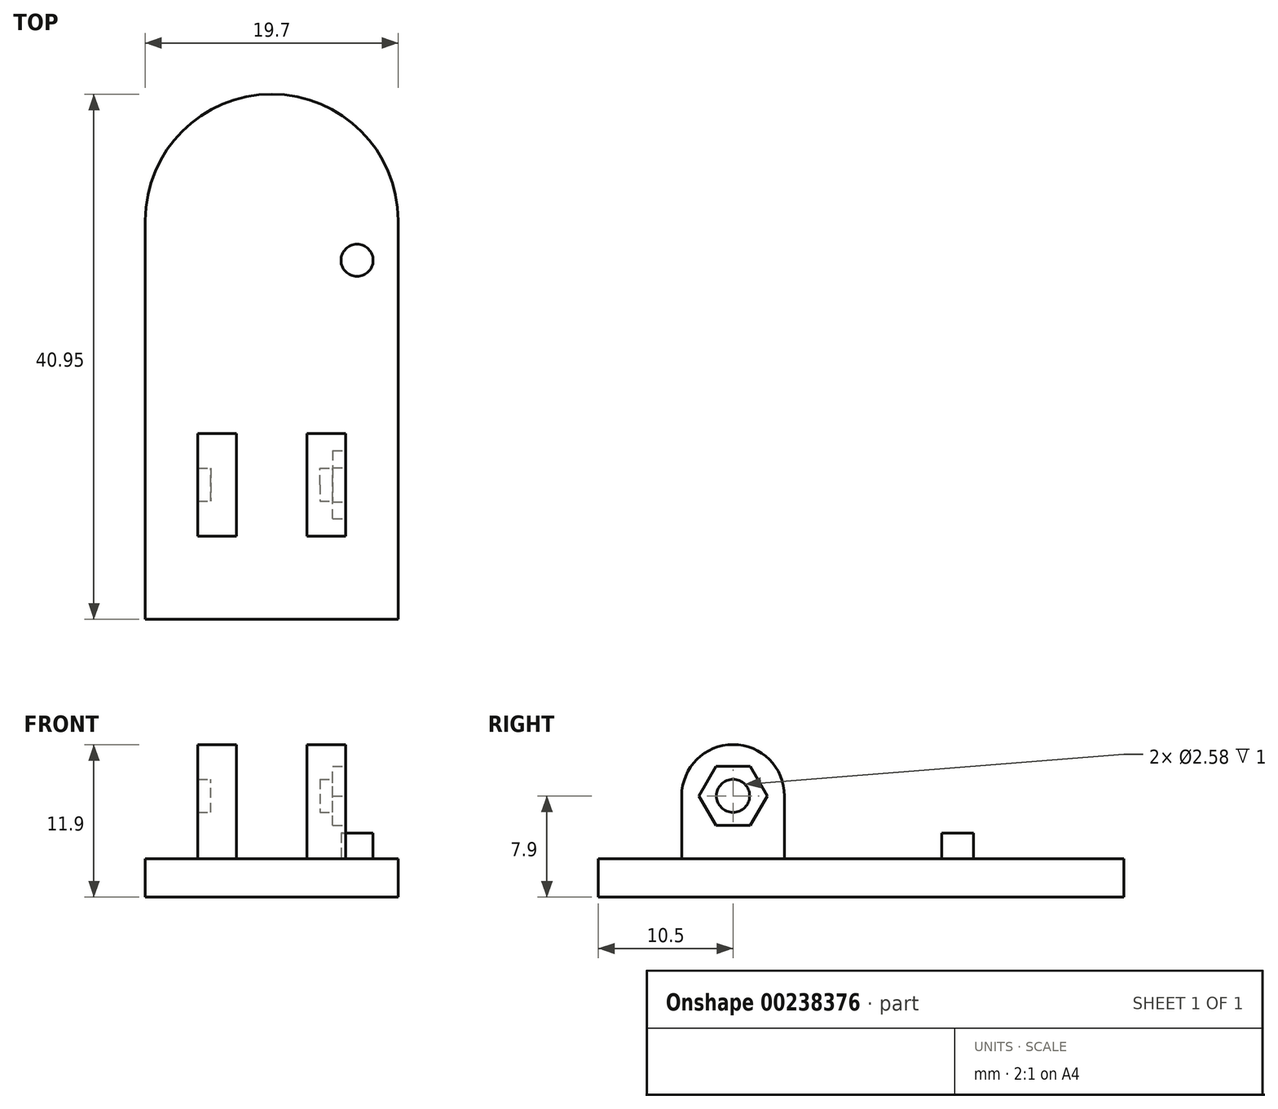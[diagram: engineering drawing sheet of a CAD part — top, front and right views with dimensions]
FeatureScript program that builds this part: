
annotation { "Feature Type Name" : "Feature", "Feature Type Description" : "" }
export const myFeature = defineFeature(function(context is Context, id is Id, definition is map)
    precondition{}
    {
        {
            var Q0;
            Q0=qCreatedBy(makeId("Top.planeOp"),FACE);
            var sketch = newSketch(context, id + "F0", { "sketchPlane" : qUnion([Q0])});
            skCircle(sketch, "E0", {"center": v(0, 0) * mm, "radius": 9.35 * mm});
            skLineSegment(sketch, "E1", {"start": v(-9.35, 0) * mm, "end": v(-9.35, -30.6) * mm});
            skLineSegment(sketch, "E2", {"start": v(9.35, 0) * mm, "end": v(9.35, -30.6) * mm});
            skLineSegment(sketch, "E3", {"start": v(9.35, -30.6) * mm, "end": v(-9.35, -30.6) * mm});
            skLineSegment(sketch, "E4", {"start": v(-5.75, -24.6) * mm, "end": v(-2.75, -24.6) * mm});
            skLineSegment(sketch, "E5.0", {"start": v(5.75, -16.6) * mm, "end": v(5.75, -24.6) * mm});
            skLineSegment(sketch, "E6.trimOffspring", {"start": v(-5.75, -16.6) * mm, "end": v(-5.75, -24.6) * mm});
            skLineSegment(sketch, "E7.0", {"start": v(-2.75, -16.6) * mm, "end": v(-2.75, -24.6) * mm});
            skLineSegment(sketch, "E8.0", {"start": v(2.75, -16.6) * mm, "end": v(2.75, -24.6) * mm});
            skLineSegment(sketch, "E9.trimOffspring", {"start": v(2.75, -16.6) * mm, "end": v(5.75, -16.6) * mm});
            skPoint(sketch, "E10.orphan", {"position": v(9.35, -16.6) * mm});
            skPoint(sketch, "E11.trimOffspring.end.orphan", {"position": v(0, 9.35) * mm});
            skLineSegment(sketch, "E12.trimOffspring", {"start": v(2.75, -24.6) * mm, "end": v(5.75, -24.6) * mm});
            skPoint(sketch, "E13.start.orphan", {"position": v(0, -30.6) * mm});
            skPoint(sketch, "E14.orphan", {"position": v(-9.35, -24.6) * mm});
            skLineSegment(sketch, "E15", {"start": v(-5.75, -16.6) * mm, "end": v(-2.75, -16.6) * mm});
            skSolve(sketch);
        }
        {
            var Q0;
            Q0=makeQuery(id+"F0.imprint","IMPRINT",FACE,{"disambiguationData":[TD([[makeQuery(id+"F0.imprint","IMPRINT",EDGE,{"derivedFrom":sQuery(id+"F0.wireOp",EDGE,"E5.0")}),-1.0]])]});
            var Q1;
            {var subQ0=sQuery(id+"F0.wireOp",EDGE,"E0");var subQ1=makeQuery(id+"F0.imprint","INTERSECT",VERTEX,{"derivedFrom":[subQ0,sQuery(id+"F0.wireOp",EDGE,"E1")]});Q1=makeQuery(id+"F0.imprint","IMPRINT",FACE,{"disambiguationData":[TD([[makeQuery(id+"F0.imprint","IMPRINT",EDGE,{"disambiguationData":[TD([[subQ1,1.0]])],"derivedFrom":subQ0}),1.0]])]});}
            var Q2;
            {var subQ1=sQuery(id+"F0.wireOp",EDGE,"E1");Q2=makeQuery(id+"F0.imprint","IMPRINT",FACE,{"disambiguationData":[TD([[makeQuery(id+"F0.imprint","IMPRINT",EDGE,{"derivedFrom":subQ1}),1.0]])]});}
            var Q3;
            Q3=makeQuery(id+"F0.imprint","IMPRINT",FACE,{"disambiguationData":[TD([[makeQuery(id+"F0.imprint","IMPRINT",EDGE,{"derivedFrom":sQuery(id+"F0.wireOp",EDGE,"E4")}),1.0]])]});
            extrude(context, id + "F1", {"entities" : qUnion([Q0, Q1, Q2, Q3]), "oppositeDirection" : true, "depth" : 3 * mm});
        }
        {
            var Q0;
            Q0=makeQuery(id+"F0.imprint","IMPRINT",FACE,{"disambiguationData":[TD([[makeQuery(id+"F0.imprint","IMPRINT",EDGE,{"derivedFrom":sQuery(id+"F0.wireOp",EDGE,"E5.0")}),-1.0]])]});
            extrude(context, id + "F2", {"entities" : qUnion([Q0]), "operationType" : NewBodyOperationType.ADD, "depth" : 4.9 * mm});
        }
        {
            var Q0;
            Q0=makeQuery(id+"F0.imprint","IMPRINT",FACE,{"disambiguationData":[TD([[makeQuery(id+"F0.imprint","IMPRINT",EDGE,{"derivedFrom":sQuery(id+"F0.wireOp",EDGE,"E4")}),1.0]])]});
            extrude(context, id + "F3", {"entities" : qUnion([Q0]), "operationType" : NewBodyOperationType.ADD, "depth" : 4.9 * mm});
        }
        {
            var Q0;
            Q0=makeQuery(id+"F3.opExtrude","SWEPT_FACE",FACE,{"disambiguationData":[OSD([sQuery(id+"F0.wireOp",EDGE,"E6.trimOffspring")])]});
            var sketch = newSketch(context, id + "F4", { "sketchPlane" : qUnion([Q0])});
            skCircle(sketch, "E16", {"center": v(20.6, 4.9) * mm, "radius": 4 * mm});
            skSolve(sketch);
        }
        {
            var Q0;
            {var subQ1=sQuery(id+"F0.wireOp",EDGE,"E6.trimOffspring");var subQ2=makeQuery(id+"F3.opExtrude","CAP_EDGE",EDGE,{"disambiguationData":[OSD([subQ1])],"isStart":false});Q0=makeQuery(id+"F4.imprint","IMPRINT",FACE,{"disambiguationData":[TD([[makeQuery(id+"F4.imprint","IMPRINT",EDGE,{"derivedFrom":subQ2}),1.0]])]});}
            extrude(context, id + "F5", {"entities" : qUnion([Q0]), "operationType" : NewBodyOperationType.ADD, "oppositeDirection" : true, "depth" : 3 * mm});
        }
        {
            var Q0;
            Q0=makeQuery(id+"F2.opExtrude","SWEPT_FACE",FACE,{"disambiguationData":[OSD([sQuery(id+"F0.wireOp",EDGE,"E5.0")])]});
            var sketch = newSketch(context, id + "F6", { "sketchPlane" : qUnion([Q0])});
            skCircle(sketch, "E17", {"center": v(-20.6, 4.9) * mm, "radius": 4 * mm});
            skCircle(sketch, "E18", {"center": v(-20.6, 4.9) * mm, "radius": 1.29 * mm});
            skCircle(sketch, "E19", {"center": v(-20.6, 4.9) * mm, "radius": 2.66 * mm, "construction": true});
            skLineSegment(sketch, "E20.0", {"start": v(-17.94, 4.9) * mm, "end": v(-19.27, 2.6) * mm});
            skLineSegment(sketch, "E20.1", {"start": v(-19.27, 2.6) * mm, "end": v(-21.93, 2.6) * mm});
            skLineSegment(sketch, "E20.2", {"start": v(-21.93, 2.6) * mm, "end": v(-23.26, 4.9) * mm});
            skLineSegment(sketch, "E20.3", {"start": v(-23.26, 4.9) * mm, "end": v(-21.93, 7.2) * mm});
            skLineSegment(sketch, "E20.4", {"start": v(-21.93, 7.2) * mm, "end": v(-19.27, 7.2) * mm});
            skLineSegment(sketch, "E20.5", {"start": v(-19.27, 7.2) * mm, "end": v(-17.94, 4.9) * mm});
            skSolve(sketch);
        }
        {
            var Q0;
            {var subQ1=sQuery(id+"F0.wireOp",EDGE,"E5.0");var subQ2=makeQuery(id+"F2.opExtrude","CAP_EDGE",EDGE,{"disambiguationData":[OSD([subQ1])],"isStart":false});Q0=makeQuery(id+"F6.imprint","IMPRINT",FACE,{"disambiguationData":[TD([[makeQuery(id+"F6.imprint","IMPRINT",EDGE,{"derivedFrom":subQ2}),-1.0]])]});}
            extrude(context, id + "F7", {"entities" : qUnion([Q0]), "operationType" : NewBodyOperationType.ADD, "oppositeDirection" : true, "depth" : 3 * mm});
        }
        {
            var Q0;
            {var subQ0=sQuery(id+"F6.wireOp",EDGE,"E18");var subQ1=makeQuery(id+"F2.opExtrude","CAP_EDGE",EDGE,{"disambiguationData":[OSD([sQuery(id+"F0.wireOp",EDGE,"E5.0")])],"isStart":false});var subQ2=makeQuery(id+"F6.imprint","INTERSECT",VERTEX,{"disambiguationData":[OD(0.0)],"derivedFrom":[subQ1,subQ0]});Q0=makeQuery(id+"F6.imprint","IMPRINT",FACE,{"disambiguationData":[TD([[makeQuery(id+"F6.imprint","IMPRINT",EDGE,{"disambiguationData":[TD([[subQ2,-1.0]])],"derivedFrom":subQ0}),1.0]])]});}
            var Q1;
            {var subQ0=sQuery(id+"F6.wireOp",EDGE,"E18");var subQ1=makeQuery(id+"F2.opExtrude","CAP_EDGE",EDGE,{"disambiguationData":[OSD([sQuery(id+"F0.wireOp",EDGE,"E5.0")])],"isStart":false});var subQ2=makeQuery(id+"F6.imprint","INTERSECT",VERTEX,{"disambiguationData":[OD(0.0)],"derivedFrom":[subQ1,subQ0]});Q1=makeQuery(id+"F6.imprint","IMPRINT",FACE,{"disambiguationData":[TD([[makeQuery(id+"F6.imprint","IMPRINT",EDGE,{"disambiguationData":[TD([[subQ2,1.0]])],"derivedFrom":subQ0}),1.0]])]});}
            extrude(context, id + "F8", {"entities" : qUnion([Q0, Q1]), "operationType" : NewBodyOperationType.REMOVE, "oppositeDirection" : true, "depth" : 25 * mm});
        }
        {
            var Q0;
            {var subQ0=sQuery(id+"F6.wireOp",EDGE,"E20.3");Q0=makeQuery(id+"F6.imprint","IMPRINT",FACE,{"disambiguationData":[TD([[makeQuery(id+"F6.imprint","IMPRINT",EDGE,{"derivedFrom":subQ0}),-1.0]])]});}
            var Q1;
            {var subQ1=sQuery(id+"F6.wireOp",EDGE,"E20.0");Q1=makeQuery(id+"F6.imprint","IMPRINT",FACE,{"disambiguationData":[TD([[makeQuery(id+"F6.imprint","IMPRINT",EDGE,{"derivedFrom":subQ1}),-1.0]])]});}
            extrude(context, id + "F9", {"entities" : qUnion([Q0, Q1]), "operationType" : NewBodyOperationType.REMOVE, "oppositeDirection" : true, "depth" : 1 * mm});
        }
        {
            var Q0;
            {var subQ0=sQuery(id+"F0.wireOp",EDGE,"E0");var subQ1=makeQuery(id+"F0.imprint","INTERSECT",VERTEX,{"derivedFrom":[subQ0,sQuery(id+"F0.wireOp",EDGE,"E1")]});Q0=makeQuery(id+"F0.imprint","IMPRINT",FACE,{"disambiguationData":[TD([[makeQuery(id+"F0.imprint","IMPRINT",EDGE,{"disambiguationData":[TD([[subQ1,1.0]])],"derivedFrom":subQ0}),1.0]])]});}
            var sketch = newSketch(context, id + "F10", { "sketchPlane" : qUnion([Q0])});
            skLineSegment(sketch, "E21.0", {"start": v(-9.35, 0) * mm, "end": v(-9.35, -30.6) * mm});
            skArc(sketch, "E21.1", {"start": v(9.35, 0) * mm, "mid": v(0, 9.35) * mm, "end": v(-9.35, 0) * mm});
            skLineSegment(sketch, "E21.2", {"start": v(9.35, 0) * mm, "end": v(9.35, -30.6) * mm});
            skLineSegment(sketch, "E21.3", {"start": v(9.35, -30.6) * mm, "end": v(-9.35, -30.6) * mm});
            skLineSegment(sketch, "E22.0", {"start": v(9.85, 0) * mm, "end": v(9.85, -31.1) * mm});
            skLineSegment(sketch, "E22.1", {"start": v(9.85, -31.1) * mm, "end": v(-9.85, -31.1) * mm});
            skLineSegment(sketch, "E22.2", {"start": v(-9.85, 0) * mm, "end": v(-9.85, -31.1) * mm});
            skArc(sketch, "E23.0", {"start": v(9.85, 0) * mm, "mid": v(0, 9.85) * mm, "end": v(-9.85, 0) * mm});
            skSolve(sketch);
        }
        {
            var Q0;
            Q0=makeQuery(id+"F10.imprint","IMPRINT",FACE,{"disambiguationData":[TD([[makeQuery(id+"F10.imprint","IMPRINT",EDGE,{"derivedFrom":sQuery(id+"F10.wireOp",EDGE,"E21.0")}),-1.0]])]});
            extrude(context, id + "F11", {"entities" : qUnion([Q0]), "operationType" : NewBodyOperationType.ADD, "oppositeDirection" : true, "depth" : 3 * mm});
        }
        {
            var Q0;
            Q0=makeQuery(id+"F5.boolean.opBoolean","MERGE",FACE,{"derivedFrom":[makeQuery(id+"F3.opExtrude","SWEPT_FACE",FACE,{"disambiguationData":[OSD([sQuery(id+"F0.wireOp",EDGE,"E7.0")])]}),makeQuery(id+"F5.opExtrude","CAP_FACE",FACE,{"disambiguationData":[OSD([sQuery(id+"F0.wireOp",EDGE,"E6.trimOffspring"),sQuery(id+"F4.wireOp",EDGE,"E16")])],"isStart":false})]});
            var sketch = newSketch(context, id + "F12", { "sketchPlane" : qUnion([Q0])});
            skCircle(sketch, "E24", {"center": v(-20.6, 4.9) * mm, "radius": 1.86 * mm});
            skSolve(sketch);
        }
        {
            var Q0;
            Q0 = qSketchRegion(id + "F12", true);
            extrude(context, id + "F13", {"entities" : qUnion([Q0]), "operationType" : NewBodyOperationType.ADD, "oppositeDirection" : true, "depth" : 1 * mm});
        }
        {
            var Q0;
            Q0=makeQuery(id+"F7.boolean.opBoolean","MERGE",FACE,{"derivedFrom":[makeQuery(id+"F2.opExtrude","SWEPT_FACE",FACE,{"disambiguationData":[OSD([sQuery(id+"F0.wireOp",EDGE,"E8.0")])]}),makeQuery(id+"F7.opExtrude","CAP_FACE",FACE,{"disambiguationData":[OSD([sQuery(id+"F0.wireOp",EDGE,"E5.0"),sQuery(id+"F6.wireOp",EDGE,"E17"),sQuery(id+"F6.wireOp",EDGE,"E18")])],"isStart":false})]});
            var sketch = newSketch(context, id + "F14", { "sketchPlane" : qUnion([Q0])});
            skCircle(sketch, "E25", {"center": v(20.6, 4.9) * mm, "radius": 1.9 * mm});
            skSolve(sketch);
        }
        {
            var Q0;
            Q0 = qSketchRegion(id + "F14", true);
            extrude(context, id + "F15", {"entities" : qUnion([Q0]), "operationType" : NewBodyOperationType.ADD, "oppositeDirection" : true, "depth" : 1 * mm});
        }
        {
            var Q0;
            Q0=makeQuery(id+"F10.imprint","IMPRINT",FACE,{"disambiguationData":[TD([[makeQuery(id+"F10.imprint","IMPRINT",EDGE,{"derivedFrom":sQuery(id+"F10.wireOp",EDGE,"E21.0")}),1.0]])]});
            var sketch = newSketch(context, id + "F16", { "sketchPlane" : qUnion([Q0])});
            skLineSegment(sketch, "E26.0", {"start": v(2.75, -16.6) * mm, "end": v(5.75, -16.6) * mm});
            skLineSegment(sketch, "E27", {"start": v(5.75, -16.6) * mm, "end": v(5.75, -3.1) * mm, "construction": true});
            skLineSegment(sketch, "E28", {"start": v(5.75, -3.1) * mm, "end": v(6.65, -3.1) * mm});
            skCircle(sketch, "E29", {"center": v(6.65, -3.1) * mm, "radius": 1.25 * mm});
            skSolve(sketch);
        }
        {
            var Q0;
            Q0 = qSketchRegion(id + "F16", true);
            extrude(context, id + "F17", {"entities" : qUnion([Q0]), "operationType" : NewBodyOperationType.ADD, "depth" : 2 * mm});
        }
        {
            var Q0;
            Q0=makeQuery(id+"F13.opExtrude","CAP_FACE",FACE,{"disambiguationData":[OSD([sQuery(id+"F12.wireOp",EDGE,"E24")])],"isStart":false});
            extrude(context, id + "F18", {"entities" : qUnion([Q0]), "operationType" : NewBodyOperationType.ADD, "depth" : 1 * mm});
        }
    });
